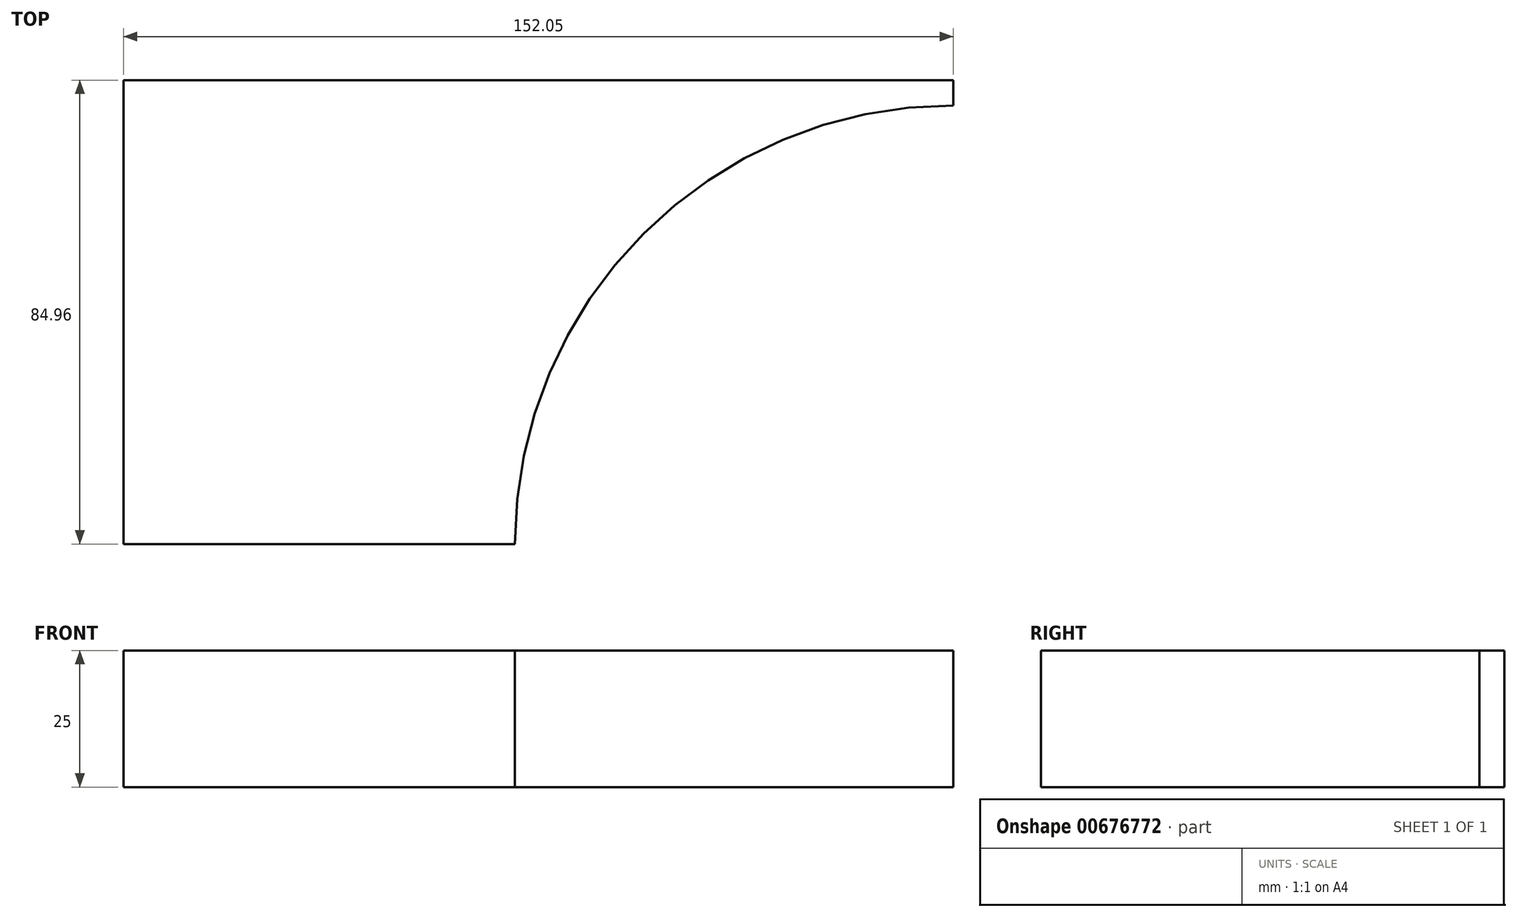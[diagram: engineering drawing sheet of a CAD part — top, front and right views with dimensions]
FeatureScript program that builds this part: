
annotation { "Feature Type Name" : "Feature", "Feature Type Description" : "" }
export const myFeature = defineFeature(function(context is Context, id is Id, definition is map)
    precondition{}
    {
        {
            var Q0;
            Q0=qCreatedBy(makeId("Top.planeOp"),FACE);
            var sketch = newSketch(context, id + "F0", { "sketchPlane" : qUnion([Q0])});
            skArc(sketch, "E0", {"start": v(0, 80.34) * mm, "mid": v(-56.81, 56.81) * mm, "end": v(-80.34, 0) * mm});
            skLineSegment(sketch, "E1.bottom", {"start": v(-80.34, 0) * mm, "end": v(-152.05, 0) * mm});
            skLineSegment(sketch, "E1.top", {"start": v(0, 84.96) * mm, "end": v(-152.05, 84.96) * mm});
            skLineSegment(sketch, "E1.left", {"start": v(0, 80.34) * mm, "end": v(0, 84.96) * mm});
            skLineSegment(sketch, "E1.right", {"start": v(-152.05, 0) * mm, "end": v(-152.05, 84.96) * mm});
            skSolve(sketch);
        }
        {
            var Q0;
            Q0=makeQuery(id+"F0.imprint","IMPRINT",FACE,{"disambiguationData":[TD([[makeQuery(id+"F0.imprint","IMPRINT",EDGE,{"derivedFrom":sQuery(id+"F0.wireOp",EDGE,"E0")}),-1.0]])]});
            extrude(context, id + "F1", {"entities" : qUnion([Q0]), "depth" : 25 * mm, "offsetDistance" : 25 * mm});
        }
    });
